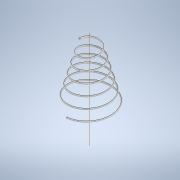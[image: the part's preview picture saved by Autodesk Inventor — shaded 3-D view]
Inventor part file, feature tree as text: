
AUTODESK INVENTOR PART (.ipt)
format: ipt  version: 2020 (Build 240168000, 168)  size: 257,536 bytes
history: native  units: mm
features: other x2, sketch x2, sweep x1
ambient origin geometry x8: Origin, YZ Plane, XZ Plane, XY Plane, X Axis, Y Axis, Z Axis, Center Point
bodies: Solid1 (feature_tree)
feature tree (5):
  sweep  "Sweep1"
  other  "Work Axis1"
  sketch  "3D Sketch1"
  other  "Helical Curve1"
  sketch  "Sketch2"  dims[d0=2.0mm d1=57.83mm d2=10.0mm d3=-2.617994mm d4=0.3mm d5=0.0mm d6=0.0mm]
